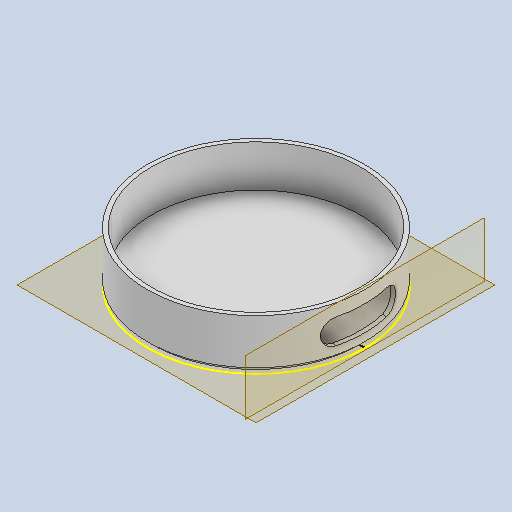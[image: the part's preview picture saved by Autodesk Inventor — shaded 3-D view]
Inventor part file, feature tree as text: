
AUTODESK INVENTOR PART (.ipt)
format: ipt  version: 2023 (Build 270158000, 158)  size: 272,896 bytes
history: native  units: in
note: dims shown in document units (in); Inventor stores cm internally (conversion verified against a paired STEP export)
features: sketch x4, extrude x3, chamfer x1, plane x1
ambient origin geometry x8: Origin, YZ Plane, XZ Plane, XY Plane, X Axis, Y Axis, Z Axis, Center Point
bodies: Solid1 (feature_tree)
feature tree (9):
  extrude  "Extrusion1"  Depth=1.1811in TaperAngle=0.0deg
  extrude  "Extrusion2"  Depth=0.9843in TaperAngle=0.0deg
  chamfer  "Chamfer1"  Distance=0.1181in Angle=45.0deg
  sketch  "Sketch4"  dims[d9=0.5906in d10=0.5906in]
  plane  "Work Plane1"
  extrude  "Extrusion3"  Depth=0.5906in
  sketch  "Sketch2"  dims[d0=5.1181in d1=1.1811in d2=0.0in]
  sketch  "Sketch3"  dims[d3=4.9213in d4=0.9843in d5=0.0in d6=0.1181in d7=0.0787in d8=45.0deg]
  sketch  "Sketch5"  dims[d11=0.3937in d12=0.0in]
